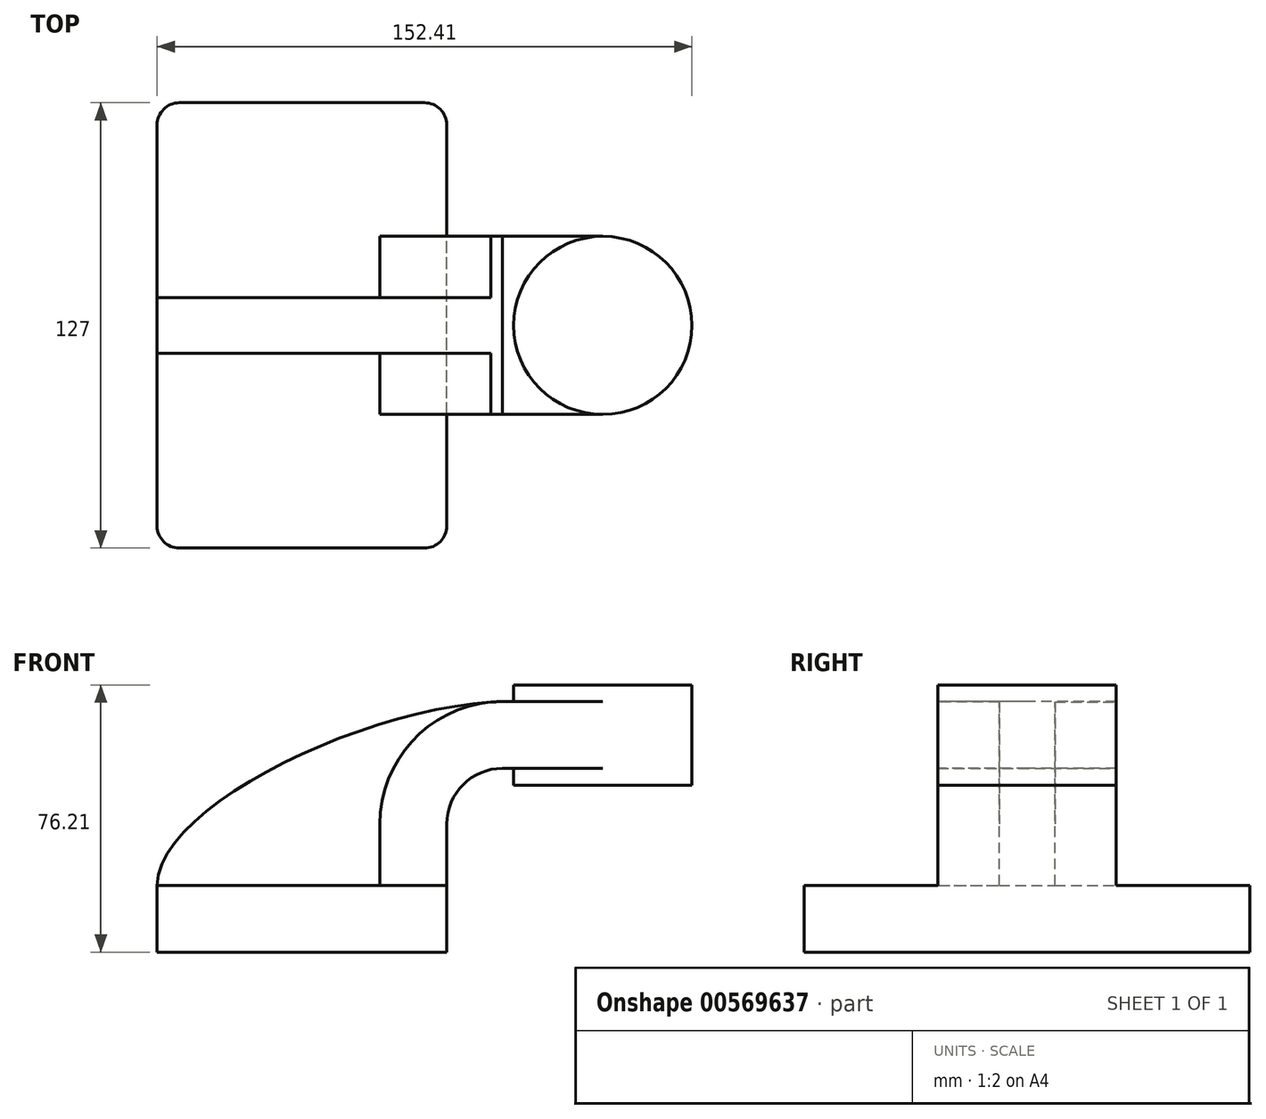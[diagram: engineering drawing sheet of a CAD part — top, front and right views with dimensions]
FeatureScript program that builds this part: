
annotation { "Feature Type Name" : "Feature", "Feature Type Description" : "" }
export const myFeature = defineFeature(function(context is Context, id is Id, definition is map)
    precondition{}
    {
        {
            var Q0;
            Q0=qCreatedBy(makeId("Front.planeOp"),FACE);
            var sketch = newSketch(context, id + "F0", { "sketchPlane" : qUnion([Q0])});
            skLineSegment(sketch, "E0.bottom", {"start": v(-41.28, -9.53) * mm, "end": v(41.28, -9.53) * mm});
            skLineSegment(sketch, "E0.top", {"start": v(-41.28, 9.53) * mm, "end": v(41.28, 9.53) * mm});
            skLineSegment(sketch, "E0.left", {"start": v(-41.28, -9.53) * mm, "end": v(-41.28, 9.53) * mm});
            skLineSegment(sketch, "E0.right", {"start": v(41.28, -9.53) * mm, "end": v(41.28, 9.53) * mm});
            skPoint(sketch, "E0.middle", {"position": v(0, 0) * mm});
            skLineSegment(sketch, "E1.bottom", {"start": v(60.32, 38.1) * mm, "end": v(111.12, 38.1) * mm});
            skLineSegment(sketch, "E1.top", {"start": v(60.32, 66.67) * mm, "end": v(111.12, 66.67) * mm});
            skLineSegment(sketch, "E1.left", {"start": v(60.32, 38.1) * mm, "end": v(60.32, 66.67) * mm});
            skLineSegment(sketch, "E1.right", {"start": v(111.12, 38.1) * mm, "end": v(111.12, 66.67) * mm});
            skPoint(sketch, "E1.middle", {"position": v(85.72, 52.39) * mm});
            skLineSegment(sketch, "E2", {"start": v(41.28, 9.53) * mm, "end": v(41.28, 27) * mm});
            skArc(sketch, "E3", {"start": v(41.28, 27) * mm, "mid": v(45.92, 38.23) * mm, "end": v(57.15, 42.88) * mm});
            skLineSegment(sketch, "E4", {"start": v(57.15, 42.88) * mm, "end": v(85.72, 42.88) * mm});
            skLineSegment(sketch, "E5.0", {"start": v(57.15, 61.93) * mm, "end": v(85.72, 61.93) * mm});
            skArc(sketch, "E5.1", {"start": v(22.23, 27) * mm, "mid": v(32.45, 51.7) * mm, "end": v(57.15, 61.93) * mm});
            skLineSegment(sketch, "E5.2", {"start": v(22.23, 9.53) * mm, "end": v(22.23, 27) * mm});
            skLineSegment(sketch, "E6", {"start": v(85.72, 38.1) * mm, "end": v(85.72, 66.67) * mm});
            skFitSpline(sketch, "E7", {"points": [v(-41.28, 9.53) * mm, v(57.15, 61.93) * mm], "startDerivative": vector(1.94, 70.17) * mm, "endDerivative": vector(113.03, 3.18) * mm});
            skSolve(sketch);
        }
        {
            var Q0;
            Q0=makeQuery(id+"F0.imprint","IMPRINT",FACE,{"disambiguationData":[TD([[makeQuery(id+"F0.imprint","IMPRINT",EDGE,{"derivedFrom":sQuery(id+"F0.wireOp",EDGE,"E0.bottom")}),1.0]])]});
            extrude(context, id + "F1", {"entities" : qUnion([Q0]), "depth" : 63.5 * mm, "offsetDistance" : 25.4 * mm, "hasSecondDirection" : true, "secondDirectionOppositeDirection" : true, "secondDirectionDepth" : 63.5 * mm});
        }
        {
            var Q0;
            {var subQ1=sQuery(id+"F0.wireOp",EDGE,"E2");Q0=makeQuery(id+"F0.imprint","IMPRINT",FACE,{"disambiguationData":[TD([[makeQuery(id+"F0.imprint","IMPRINT",EDGE,{"derivedFrom":subQ1}),1.0]])]});}
            var Q1;
            {var subQ0=sQuery(id+"F0.wireOp",EDGE,"E4");var subQ1=sQuery(id+"F0.wireOp",EDGE,"E1.left");var subQ2=makeQuery(id+"F0.imprint","INTERSECT",VERTEX,{"derivedFrom":[subQ1,subQ0]});Q1=makeQuery(id+"F0.imprint","IMPRINT",FACE,{"disambiguationData":[TD([[makeQuery(id+"F0.imprint","IMPRINT",EDGE,{"disambiguationData":[TD([[subQ2,-1.0]])],"derivedFrom":subQ1}),-1.0]])]});}
            extrude(context, id + "F2", {"entities" : qUnion([Q0, Q1]), "operationType" : NewBodyOperationType.ADD, "depth" : 25.4 * mm, "offsetDistance" : 25.4 * mm, "hasSecondDirection" : true, "secondDirectionOppositeDirection" : true, "secondDirectionDepth" : 25.4 * mm});
        }
        {
            var Q0;
            {var subQ3=sQuery(id+"F0.wireOp",EDGE,"E5.2");Q0=makeQuery(id+"F0.imprint","IMPRINT",FACE,{"disambiguationData":[TD([[makeQuery(id+"F0.imprint","IMPRINT",EDGE,{"derivedFrom":subQ3}),1.0]])]});}
            extrude(context, id + "F3", {"entities" : qUnion([Q0]), "operationType" : NewBodyOperationType.ADD, "endBound" : BoundingType.SYMMETRIC, "depth" : 15.88 * mm, "offsetDistance" : 25.4 * mm, "hasSecondDirection" : true, "secondDirectionOppositeDirection" : true, "secondDirectionDepth" : 12.7 * mm});
        }
        {
            var Q0;
            {var subQ4=sQuery(id+"F0.wireOp",EDGE,"E1.right");Q0=makeQuery(id+"F0.imprint","IMPRINT",FACE,{"disambiguationData":[TD([[makeQuery(id+"F0.imprint","IMPRINT",EDGE,{"derivedFrom":subQ4}),1.0]])]});}
            var Q1;
            Q1=sQuery(id+"F0.wireOp",EDGE,"E6");
            revolve(context, id + "F4", {"operationType" : NewBodyOperationType.ADD, "entities" : qUnion([Q0]), "axis" : qUnion([Q1]), "revolveType" : RevolveType.FULL});
        }
        {
            var Q0;
            Q0=makeQuery(id+"F1.opExtrude","CAP_EDGE",EDGE,{"disambiguationData":[OSD([sQuery(id+"F0.wireOp",EDGE,"E0.right")])],"isStart":false});
            var Q1;
            Q1=makeQuery(id+"F1.opExtrude","CAP_EDGE",EDGE,{"disambiguationData":[OSD([sQuery(id+"F0.wireOp",EDGE,"E0.left")])],"isStart":false});
            var Q2;
            Q2=makeQuery(id+"F1.opExtrude","CAP_EDGE",EDGE,{"disambiguationData":[OSD([sQuery(id+"F0.wireOp",EDGE,"E0.left")])],"isStart":true});
            var Q3;
            Q3=makeQuery(id+"F1.opExtrude","CAP_EDGE",EDGE,{"disambiguationData":[OSD([sQuery(id+"F0.wireOp",EDGE,"E0.right")])],"isStart":true});
            fillet(context, id + "F5", {"entities" : qUnion([Q0, Q1, Q2, Q3]), "radius" : 6.35 * mm, "tangentPropagation" : true, "allowEdgeOverflow" : false});
        }
    });
